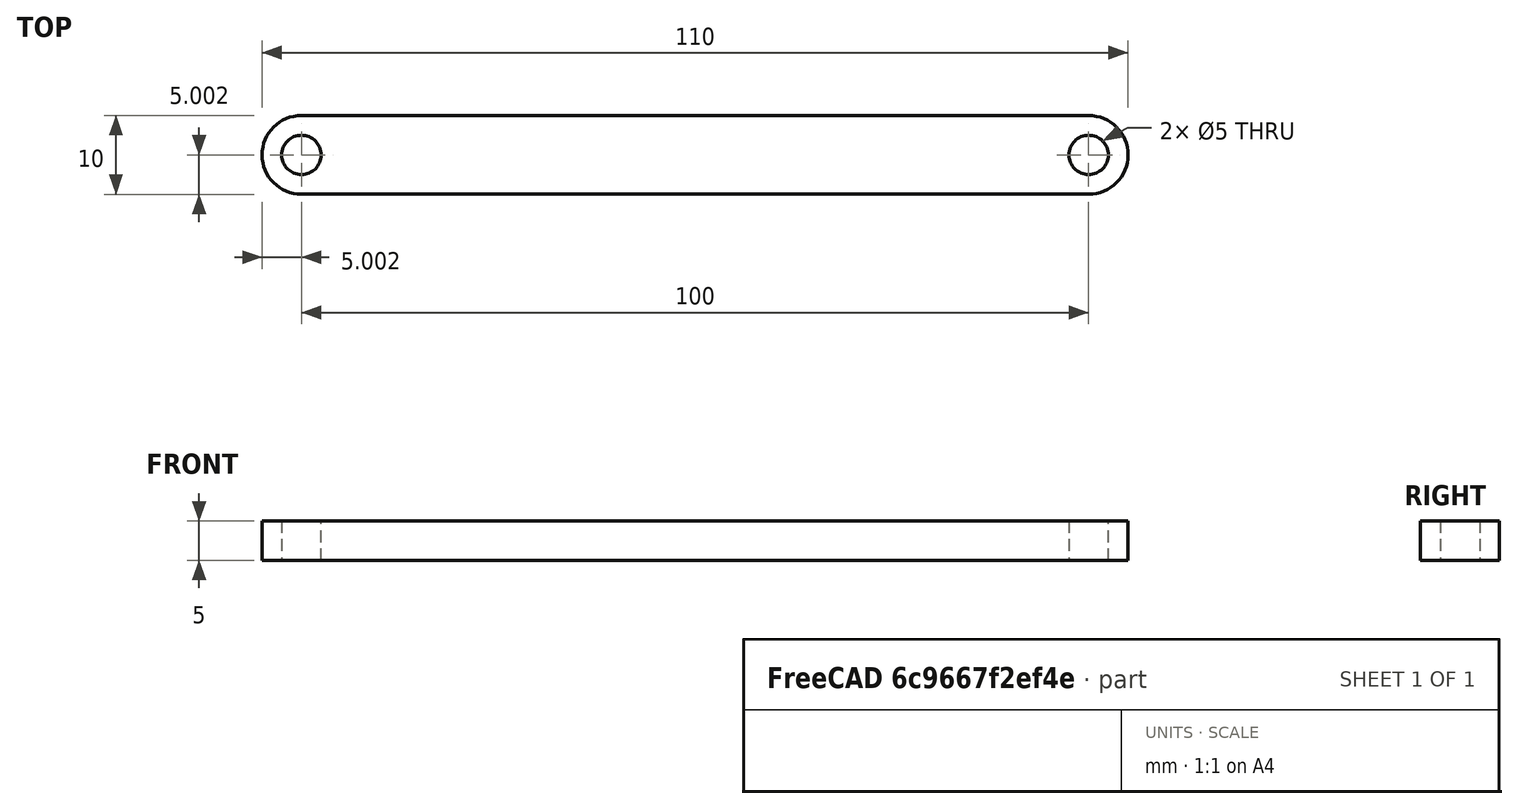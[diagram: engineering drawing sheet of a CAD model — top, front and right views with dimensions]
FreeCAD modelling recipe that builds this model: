
FCSTD DOCUMENT  (FreeCAD 0.19R)
Label: BARRA-01
License: All rights reserved
LicenseURL: http://en.wikipedia.org/wiki/All_rights_reserved
objects: Sketcher::SketchObject×1, Part::Extrusion×1, App::Part×1
note: 2 computed .brp shape members not serialized (recipe doc carries the construction recipe); baked Part::Feature solids carry a one-line shape summary decoded from their .brp

FEATURE [Sketcher::SketchObject] Sketch
  FullyConstrained = false
  sketch-geometry (9):
    g0: Circle CenterX=0 CenterY=0 CenterZ=0 NormalX=0 NormalY=0 NormalZ=1 AngleXU=0 Radius=2.5
    g1: ArcOfCircle CenterX=0 CenterY=0 CenterZ=0 NormalX=0 NormalY=0 NormalZ=1 AngleXU=0 Radius=5 StartAngle=1.5708 EndAngle=4.71239
    g2: LineSegment StartX=0 StartY=0 StartZ=0 EndX=100 EndY=0 EndZ=0
    g3: Circle CenterX=100 CenterY=0 CenterZ=0 NormalX=0 NormalY=0 NormalZ=1 AngleXU=0 Radius=2.5
    g4: ArcOfCircle CenterX=100 CenterY=0 CenterZ=0 NormalX=0 NormalY=0 NormalZ=1 AngleXU=0 Radius=5 StartAngle=4.71239 EndAngle=7.85398
    g5: LineSegment StartX=3e-16 StartY=5 StartZ=0 EndX=100 EndY=5 EndZ=0
    g6: LineSegment StartX=100 StartY=5 StartZ=0 EndX=100 EndY=-5 EndZ=0
    g7: LineSegment StartX=100 StartY=-5 StartZ=0 EndX=0 EndY=-5 EndZ=0
    g8: LineSegment StartX=0 StartY=-5 StartZ=0 EndX=3e-16 EndY=5 EndZ=0
  constraints (20):
    c: Coincident(g0,g-1)
    c: Coincident(g1,g0)
    c: Coincident(g2,g0)
    c: Horizontal(g2)
    c: Coincident(g3,g2)
    c: Coincident(g4,g3)
    c: Equal(g4,g1)
    c: Equal(g0,g3)
    c: Coincident(g5,g6)
    c: Coincident(g6,g7)
    c: Coincident(g7,g8)
    c: Coincident(g8,g5)
    c: Vertical(g6)
    c: Symmetric(g6,g6,g3)
    c: Symmetric(g8,g8,g0)
    c: Coincident(g4,g5)
    c: Coincident(g1,g5)
    c: DistanceX(g2,g2) = 100
    c: Diameter(g0) = 5
    c: Diameter(g1) = 10
FEATURE [Part::Extrusion] Extrude
  Base = -> Sketch
  Dir = (0,0,1)
  DirMode = 2
  FaceMakerClass = Part::FaceMakerBullseye
  LengthFwd = 5
  LengthRev = 0
  Placement = pos=(68.7621,37.7323,-2.43325) rot=(0,0,1;0rad)
  Solid = true
  Symmetric = false
FEATURE [App::Part] Part
  Group = -> [Sketch,Extrude]
  Origin = -> Origin
